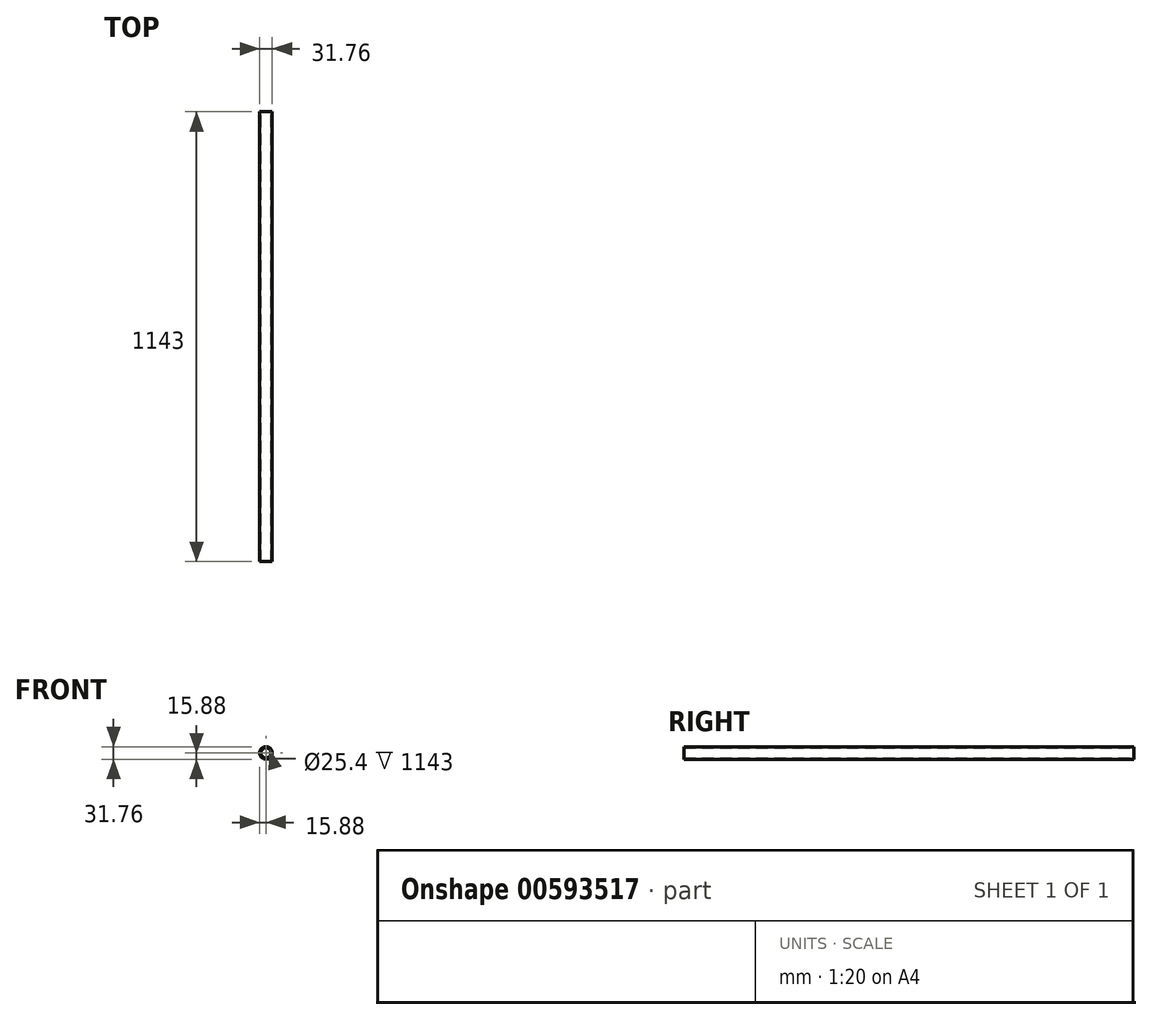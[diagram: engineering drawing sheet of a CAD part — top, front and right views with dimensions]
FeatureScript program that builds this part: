
annotation { "Feature Type Name" : "Feature", "Feature Type Description" : "" }
export const myFeature = defineFeature(function(context is Context, id is Id, definition is map)
    precondition{}
    {
        {
            var Q0;
            Q0=qCreatedBy(makeId("Front.planeOp"),FACE);
            var sketch = newSketch(context, id + "F0", { "sketchPlane" : qUnion([Q0])});
            skCircle(sketch, "E0", {"center": v(0, 0) * mm, "radius": 15.88 * mm});
            skCircle(sketch, "E1", {"center": v(0, 0) * mm, "radius": 12.7 * mm});
            skSolve(sketch);
        }
        {
            var Q0;
            Q0 = qSketchRegion(id + "F0", true);
            extrude(context, id + "F1", {"entities" : qUnion([Q0]), "depth" : 1143 * mm, "offsetDistance" : 25.4 * mm});
        }
    });
